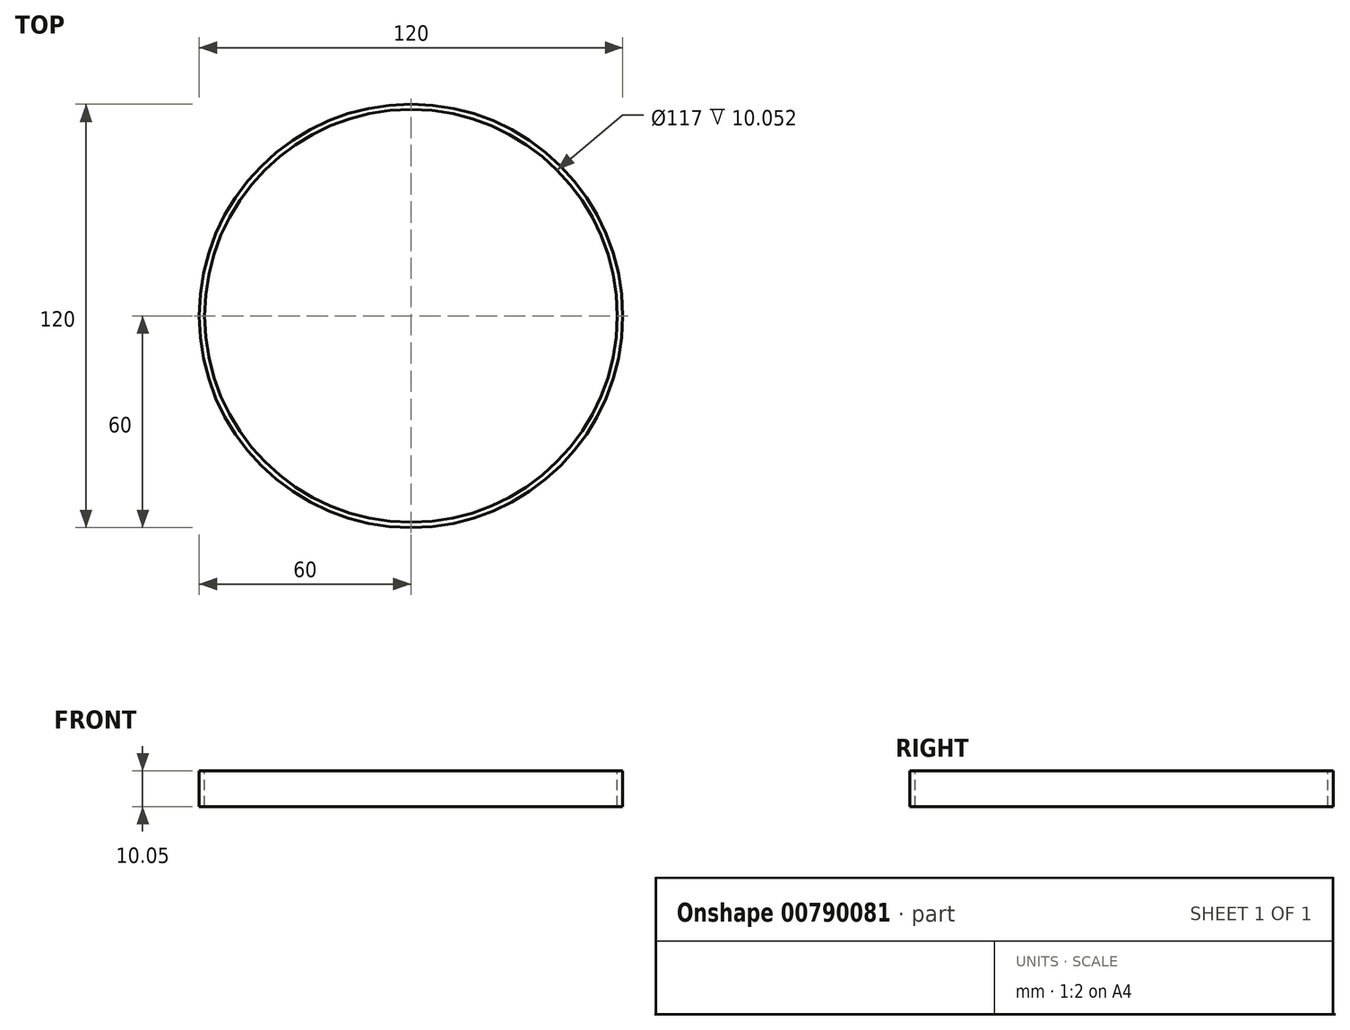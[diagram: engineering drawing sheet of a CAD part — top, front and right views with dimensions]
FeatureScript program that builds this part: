
annotation { "Feature Type Name" : "Feature", "Feature Type Description" : "" }
export const myFeature = defineFeature(function(context is Context, id is Id, definition is map)
    precondition{}
    {
        {
            var Q0;
            Q0=qCreatedBy(makeId("Top.planeOp"),FACE);
            var sketch = newSketch(context, id + "F0", { "sketchPlane" : qUnion([Q0])});
            skCircle(sketch, "E0", {"center": v(0, 0) * mm, "radius": 60 * mm});
            skCircle(sketch, "E1.0", {"center": v(0, 0) * mm, "radius": 58.5 * mm});
            skCircle(sketch, "E2.0", {"center": v(0, 0) * mm, "radius": 50.3 * mm});
            skSolve(sketch);
        }
        {
            var Q0;
            Q0 = qSketchRegion(id + "F0", true);
            var sketch = newSketch(context, id + "F1", { "sketchPlane" : qUnion([Q0])});
            skSolve(sketch);
        }
        {
            var Q0;
            Q0 = qSketchRegion(id + "F0", true);
            var Q1;
            Q1=makeQuery(id+"F1.imprint","IMPRINT",FACE,{"disambiguationData":[TD([[makeQuery(id+"F1.imprint","IMPRINT",EDGE,{"derivedFrom":makeQuery(id+"F0.imprint","IMPRINT",EDGE,{"derivedFrom":sQuery(id+"F0.wireOp",EDGE,"E1.0")})}),1.0]])]});
            extrude(context, id + "F2", {"entities" : qUnion([Q0, Q1]), "oppositeDirection" : true, "depth" : 10.05 * mm, "offsetDistance" : 25 * mm});
        }
    });
